# Revit family: PRD_AR_SpDspnsrs_RODANSoapDispenser_RODX619E
name_source: partatom
category: Specialty Equipment
revit_build: Autodesk Revit 2018 (Build: 20190510_1515(x64)
units: mm (PartAtom-declared; Revit-internal decimal feet)

## family parameters
Cut with Voids When Loaded = Yes
Host = Face
OmniClass Number = 23.40.20.21.34
OmniClass Title = Soap Holders, Dispensers
Part Type = Normal
Room Calculation Point = No
Round Connector Dimension = Use Diameter
Shared = No

## types (1)
- RODX619E
    AssetType = Fixed
    BIMObjectName = PRD_AR_SoapDispensers_RODANSoapDispenser_RODX619E
    Category = Pr_40_70_22_81, Soap dispensers
    Default Elevation = 850 mm  [stored 2.78871 ft]
    Description = Soap dispenser for recessed mounting, stainless steel, surface satin finished, material thickness 0.8 mm, folded front cover, cylinder lock with KWC standard key, suitable for liquid soaps and lotions, 1 liter soap tank, push button on front, includes stainless steel screws and dowels.
    DispenserMaterial = PRD_AR_StainlessSteel_SatinFinished
    DurationUnit = year
    Features = stainless steel, satin finished
    FillingQuantity = 1
    FillingQuantityUom = Liter
    Finish = Satin finished
    GrossWeight = 2.08 kg
    IfcExportAs = IfcFurnitureType
    IfcExportType = USERDEFINED
    IntegralAccessories = incl. stainless steel screws and dowels
    IsBuiltIn = TRUE
    Lock = Key-lock
    MainColor = Stainless steel
    Manufacturer = KWC Group AG
    ManufacturerName = KWC Group AG
    ManufacturerURL = www.kwc.com
    Material = Stainless steel
    MaterialCode = 1.4301
    MaterialThickness = 0.80 mm
    Model = RODX619E
    ModelNumber = 2000090069
    ModelReference = RODX619E
    NBSDescription = Soap dispensers
    NBSReference = 45-35-72/358
    Name = Soap dispenser RODX619E
    NetWeight = 1.85 kg
    NominalDepth = 132 mm  [stored 0.433071 ft]
    NominalHeight = 243 mm  [stored 0.797244 ft]
    NominalWidth = 241 mm  [stored 0.790682 ft]
    Offset = 0 mm  [stored 0 ft]
    ProductInformation = https://pim.kwc.com
    Size = 241 x 243 x 132 mm
    Style = Dispenser
    TypeOfConsumable = Liquid soap
    TypeOfFixing = Screw
    TypeOfMounting = Recessed mounting
    TypeOfOperation = Manual operation
    TypeOfSoapContainer = Integrated refillable tank
    URL = www.kwc.com
    Uniclass2015Code = Pr_40_70_22_81
    Uniclass2015Title = Soap dispenser
    Uniclass2015Version = Products v1.17
    Version = 1
    WarrantyDurationUnit = year

note: [stored X ft] marks values corroborated as IEEE doubles in the binary element streams (Revit-internal decimal feet)

## geometry (parser evidence)
native form markers: Sweep x5
no freeform markers — native parametric forms only
